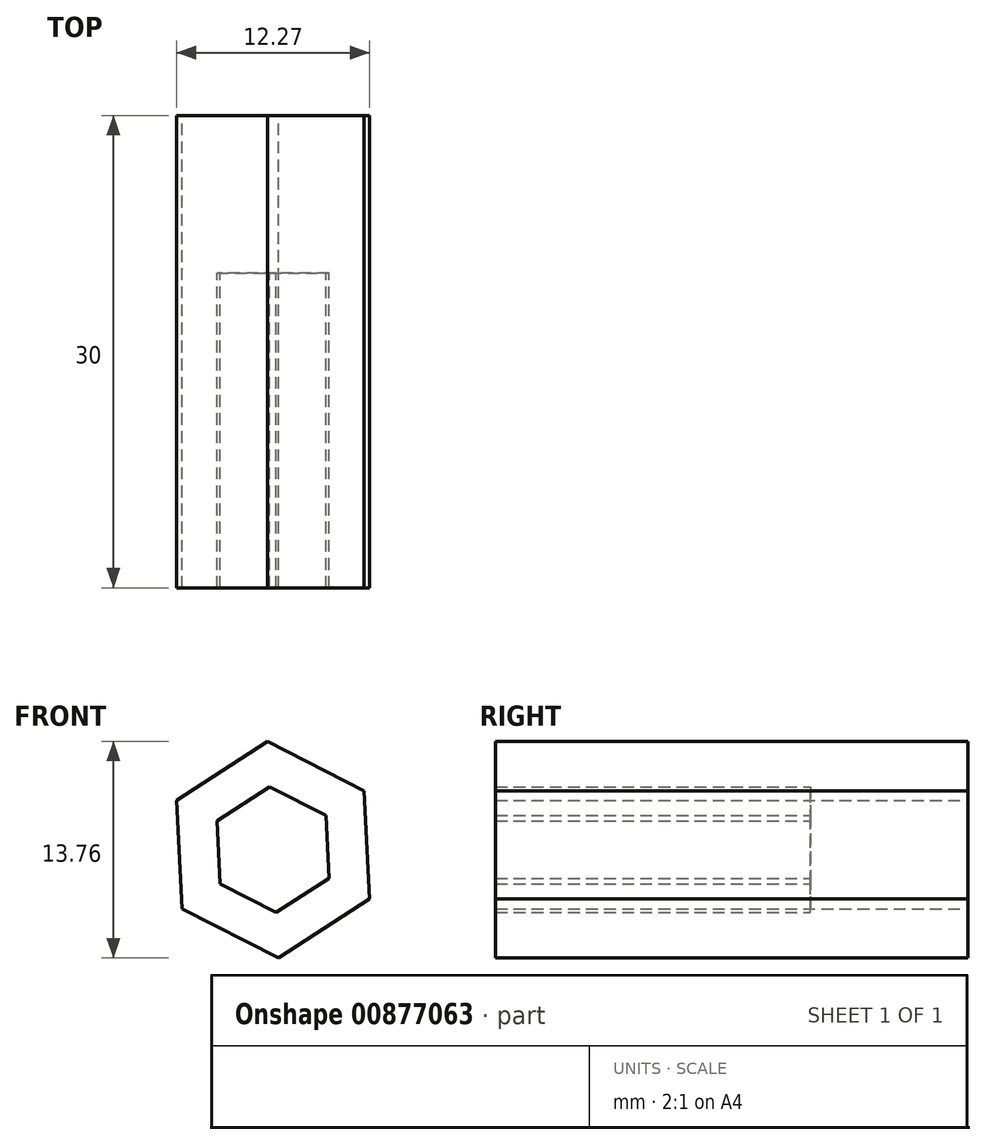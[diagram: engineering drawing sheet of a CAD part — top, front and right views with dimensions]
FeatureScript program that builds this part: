
annotation { "Feature Type Name" : "Feature", "Feature Type Description" : "" }
export const myFeature = defineFeature(function(context is Context, id is Id, definition is map)
    precondition{}
    {
        {
            var Q0;
            Q0=qCreatedBy(makeId("Front.planeOp"),FACE);
            var sketch = newSketch(context, id + "F0", { "sketchPlane" : qUnion([Q0])});
            skCircle(sketch, "E0.cCircle", {"center": v(-27.54, 18.1) * mm, "radius": 3.46 * mm, "construction": true});
            skLineSegment(sketch, "E0.0", {"start": v(-23.98, 16.3) * mm, "end": v(-27.33, 14.11) * mm});
            skLineSegment(sketch, "E0.1", {"start": v(-27.33, 14.11) * mm, "end": v(-30.9, 15.93) * mm});
            skLineSegment(sketch, "E0.2", {"start": v(-30.9, 15.93) * mm, "end": v(-31.1, 19.93) * mm});
            skLineSegment(sketch, "E0.3", {"start": v(-31.1, 19.93) * mm, "end": v(-27.75, 22.1) * mm});
            skLineSegment(sketch, "E0.4", {"start": v(-27.75, 22.1) * mm, "end": v(-24.19, 20.29) * mm});
            skLineSegment(sketch, "E0.5", {"start": v(-24.19, 20.29) * mm, "end": v(-23.98, 16.3) * mm});
            skPoint(sketch, "E0.0.midPoint", {"position": v(-25.66, 15.2) * mm});
            skLineSegment(sketch, "E1.0", {"start": v(-33.68, 21.24) * mm, "end": v(-27.9, 24.99) * mm});
            skLineSegment(sketch, "E1.1", {"start": v(-21.76, 21.86) * mm, "end": v(-21.4, 14.98) * mm});
            skLineSegment(sketch, "E1.2", {"start": v(-21.4, 14.98) * mm, "end": v(-27.18, 11.23) * mm});
            skLineSegment(sketch, "E1.3", {"start": v(-27.9, 24.99) * mm, "end": v(-21.76, 21.86) * mm});
            skLineSegment(sketch, "E1.4", {"start": v(-27.18, 11.23) * mm, "end": v(-33.32, 14.36) * mm});
            skLineSegment(sketch, "E1.5", {"start": v(-33.32, 14.36) * mm, "end": v(-33.68, 21.24) * mm});
            skSolve(sketch);
        }
        {
            var Q0;
            Q0 = qSketchRegion(id + "F0", true);
            extrude(context, id + "F1", {"entities" : qUnion([Q0]), "depth" : 30 * mm, "offsetDistance" : 25.4 * mm});
        }
        {
            var Q0;
            Q0=makeQuery(id+"F0.imprint","IMPRINT",FACE,{"disambiguationData":[TD([[makeQuery(id+"F0.imprint","IMPRINT",EDGE,{"derivedFrom":sQuery(id+"F0.wireOp",EDGE,"E0.0")}),-1.0]])]});
            extrude(context, id + "F2", {"entities" : qUnion([Q0]), "operationType" : NewBodyOperationType.ADD, "depth" : 10 * mm, "offsetDistance" : 25.4 * mm});
        }
    });
